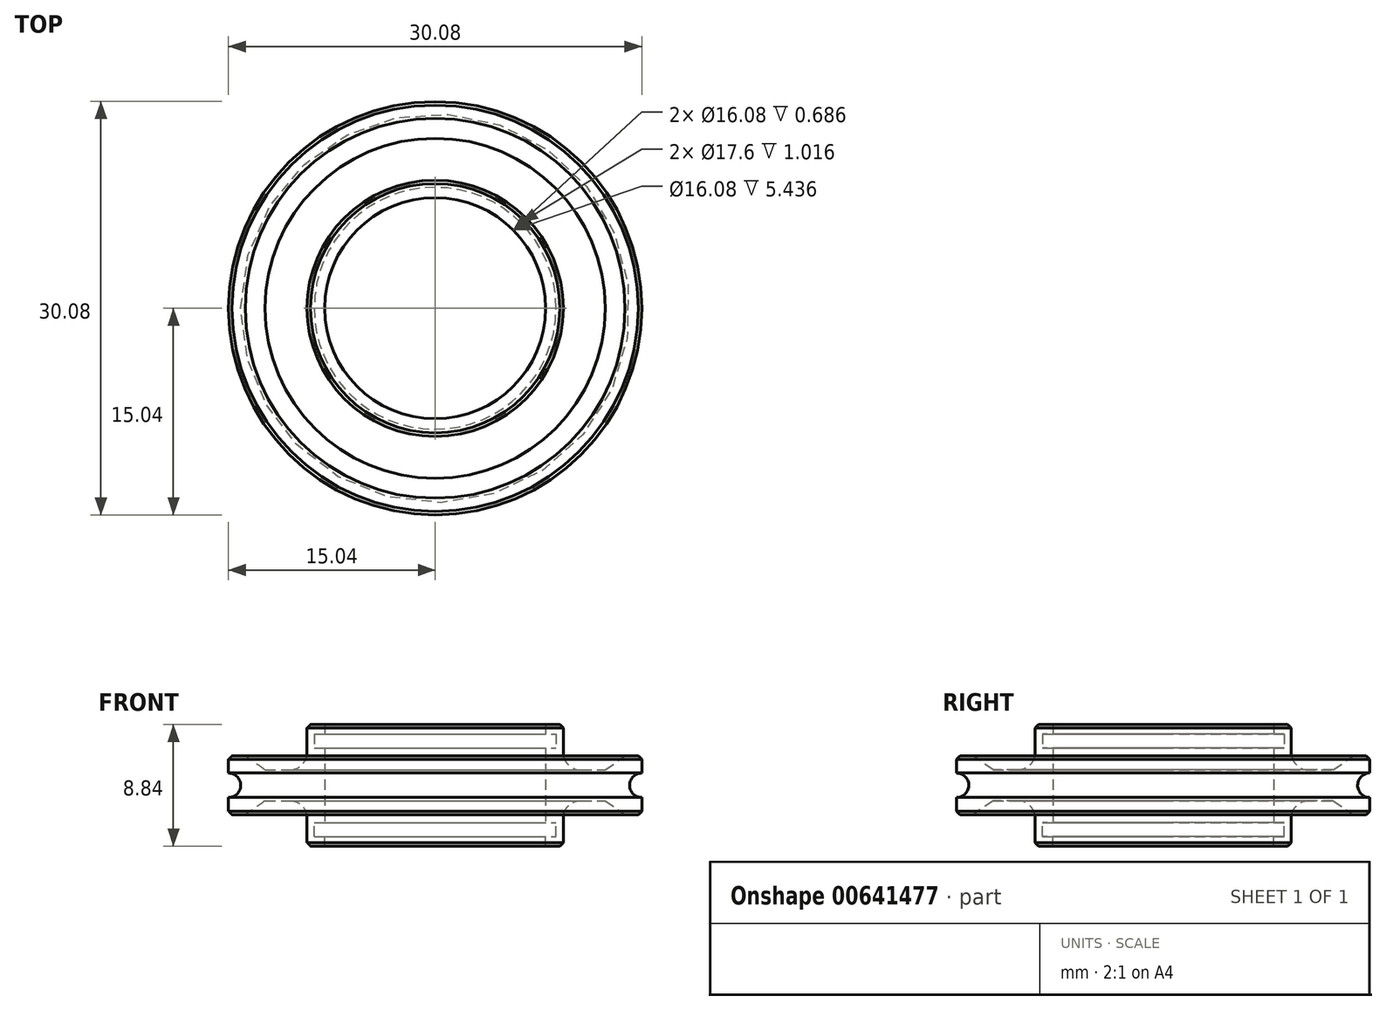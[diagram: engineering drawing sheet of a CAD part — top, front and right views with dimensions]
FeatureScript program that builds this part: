
annotation { "Feature Type Name" : "Feature", "Feature Type Description" : "" }
export const myFeature = defineFeature(function(context is Context, id is Id, definition is map)
    precondition{}
    {
        {
            var Q0;
            Q0=qCreatedBy(makeId("Front.planeOp"),FACE);
            var sketch = newSketch(context, id + "F0", { "sketchPlane" : qUnion([Q0])});
            skLineSegment(sketch, "E0", {"start": v(0, 0) * mm, "end": v(0, 36.05) * mm, "construction": true});
            skLineSegment(sketch, "E1", {"start": v(8.04, 0) * mm, "end": v(8.04, 2.72) * mm});
            skLineSegment(sketch, "E2", {"start": v(8.04, 4.42) * mm, "end": v(9.32, 4.42) * mm});
            skLineSegment(sketch, "E3", {"start": v(9.32, 4.42) * mm, "end": v(9.32, 1.12) * mm});
            skLineSegment(sketch, "E4", {"start": v(9.32, 1.12) * mm, "end": v(12.37, 1.12) * mm});
            skLineSegment(sketch, "E5", {"start": v(12.37, 1.12) * mm, "end": v(13.82, 2.13) * mm});
            skLineSegment(sketch, "E6", {"start": v(13.82, 2.13) * mm, "end": v(15.04, 2.13) * mm});
            skLineSegment(sketch, "E7", {"start": v(15.04, 2.13) * mm, "end": v(15.04, 0) * mm});
            skLineSegment(sketch, "E8", {"start": v(15.04, 0) * mm, "end": v(8.04, 0) * mm});
            skLineSegment(sketch, "E9", {"start": v(51.12, 0) * mm, "end": v(0, 0) * mm, "construction": true});
            skLineSegment(sketch, "E10", {"start": v(8.04, 3.73) * mm, "end": v(8.8, 3.73) * mm});
            skLineSegment(sketch, "E11", {"start": v(8.8, 3.73) * mm, "end": v(8.8, 2.72) * mm});
            skLineSegment(sketch, "E12", {"start": v(8.8, 2.72) * mm, "end": v(8.04, 2.72) * mm});
            skLineSegment(sketch, "E13.trimOffspring", {"start": v(8.04, 3.73) * mm, "end": v(8.04, 4.42) * mm});
            skSolve(sketch);
        }
        {
            var Q0;
            Q0=makeQuery(id+"F0.imprint","IMPRINT",FACE,{"disambiguationData":[TD([[makeQuery(id+"F0.imprint","IMPRINT",EDGE,{"derivedFrom":sQuery(id+"F0.wireOp",EDGE,"E1")}),-1.0]])]});
            var Q1;
            Q1=sQuery(id+"F0.wireOp",EDGE,"E0");
            revolve(context, id + "F1", {"entities" : qUnion([Q0]), "axis" : qUnion([Q1]), "revolveType" : RevolveType.FULL});
        }
        {
            var Q0;
            Q0=qCreatedBy(makeId("Front.planeOp"),FACE);
            var sketch = newSketch(context, id + "F2", { "sketchPlane" : qUnion([Q0])});
            skCircle(sketch, "E14", {"center": v(15.04, 0) * mm, "radius": 0.89 * mm});
            skSolve(sketch);
        }
        {
            var Q0;
            Q0 = qSketchRegion(id + "F2", true);
            var Q1;
            Q1=sQuery(id+"F0.wireOp",EDGE,"E0");
            revolve(context, id + "F3", {"operationType" : NewBodyOperationType.REMOVE, "entities" : qUnion([Q0]), "axis" : qUnion([Q1]), "revolveType" : RevolveType.FULL, "oppositeDirection" : true});
        }
        {
            var Q0;
            Q0=makeQuery(id+"F1.opRevolve","SWEPT_EDGE",EDGE,{"disambiguationData":[OSD([sQuery(id+"F0.wireOp",EDGE,"E6"),sQuery(id+"F0.wireOp",EDGE,"E7")])]});
            var Q1;
            Q1=makeQuery(id+"F1.opRevolve","SWEPT_EDGE",EDGE,{"disambiguationData":[OSD([sQuery(id+"F0.wireOp",EDGE,"E2"),sQuery(id+"F0.wireOp",EDGE,"E3")])]});
            chamfer(context, id + "F4", {"entities" : qUnion([Q0, Q1]), "width" : 0.25 * mm, "tangentPropagation" : true});
        }
        {
            var Q0;
            Q0=makeQuery(id+"F1.opRevolve","SWEPT_EDGE",EDGE,{"disambiguationData":[OSD([sQuery(id+"F0.wireOp",EDGE,"E3"),sQuery(id+"F0.wireOp",EDGE,"E4")])]});
            fillet(context, id + "F5", {"entities" : qUnion([Q0]), "radius" : 1.27 * mm, "tangentPropagation" : true, "allowEdgeOverflow" : false});
        }
        {
            var Q0;
            Q0=makeQuery(id+"F1.opRevolve","SWEPT_BODY",BODY,{"disambiguationData":[OSD([sQuery(id+"F0.wireOp",EDGE,"E1"),sQuery(id+"F0.wireOp",EDGE,"E2"),sQuery(id+"F0.wireOp",EDGE,"E3"),sQuery(id+"F0.wireOp",EDGE,"E4"),sQuery(id+"F0.wireOp",EDGE,"E5"),sQuery(id+"F0.wireOp",EDGE,"E6"),sQuery(id+"F0.wireOp",EDGE,"E7"),sQuery(id+"F0.wireOp",EDGE,"E8")])]});
            var Q1;
            Q1=qCreatedBy(makeId("Top.planeOp"),FACE);
            mirror(context, id + "F6", {"operationType" : NewBodyOperationType.ADD, "entities" : qUnion([Q0]), "mirrorPlane" : qUnion([Q1])});
        }
    });
